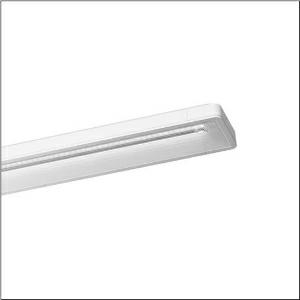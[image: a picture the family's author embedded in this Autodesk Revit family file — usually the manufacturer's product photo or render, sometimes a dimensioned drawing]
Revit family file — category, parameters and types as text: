
# Revit family: taris_r__21_5mt217703wd_caa9
name_source: partatom
category: Lighting Fixtures
units: mm (PartAtom-declared; Revit-internal decimal feet)

## family parameters
Cut with Voids When Loaded = No
Host = Face
Light Source = No
Part Type = Normal
Room Calculation Point = No
Round Connector Dimension = Use Diameter
Shared = No

## types (1)
- Taris® 21 (1 x LED, 5700 lm, 37 W, 3000K)
    Apparent Load = 37 VA
    CIE Flux Codes = 73 96 99 100 100
    Color Rendering = 80
    Color Temperature = 3000K
    Default Elevation = 1800 mm
    Description = Taris® 21, office luminaire, primary anti-glare with micro louvre, primary optical cover: axial lens, of PMMA, structured, CAT 2 (L<= 1500cd/m²), light emission: direct distribution, primary light characteristic: symmetric, installation type: surface-mounted, LED rated luminous flux: 5.700 lm, light colour: 830, colour temperature: 3000K, control gear: ECG, with terminal, 5-pole, mains connection: 230V, AC, 50Hz, rated input power: 37W, housing, luminaire housing, of plastic, traffic white (RAL 9016), length: 1.510 mm, width: 134 mm, height: 50mm, protection rating (complete): IP20, insulation class (complete): insulation class I (protective earthing), certification: CE, ENEC, VDE, protection symbol: F, impact resistance: IK02, permissible ambient temperature for indoor applications: 0..+35°C, standard: EN 50419, packaging unit: 1 piece
    Height = 51 mm
    Lamp = 1 x LED
    Lamp Light Flux = 5700 lm
    Lamp Power = 37 W
    Lamp count = 1
    Length = 1514 mm
    Luminous efficacy = 154 lm/W
    Manufacturer = Siteco
    ModVariant = No
    Model = 5MT217703WD
    Mounting Place = Ceiling
    Mounting Type = Surface mounted
    Number of Poles = 1
    OnlyDefault = Yes
    Power Factor = 1
    Product Name = Taris® 21
    Product group = office luminaire | ceiling mounted
    ProductGroupID = 302
    Protection Class = Protection class I
    Protection Degree = IP 20
    RLX_Detail_Level = 1
    RlxData = <blob elided: 38861 chars, md5=f1329047>
    Socket = socket
    Standby Power = 0 W
    System Light Flux = 5700 lm
    System Power = 37 W
    Type Comments = Product without accessories
    Type Image = l_1004728.jpg
    URL = http://relux.com
    VarID = ---
    Voltage = 0 V
    Weight = 0.00 kg
    Width = 134 mm

## geometry (parser evidence)
native form markers: Blend x4, Sweep x10
no freeform markers — native parametric forms only
